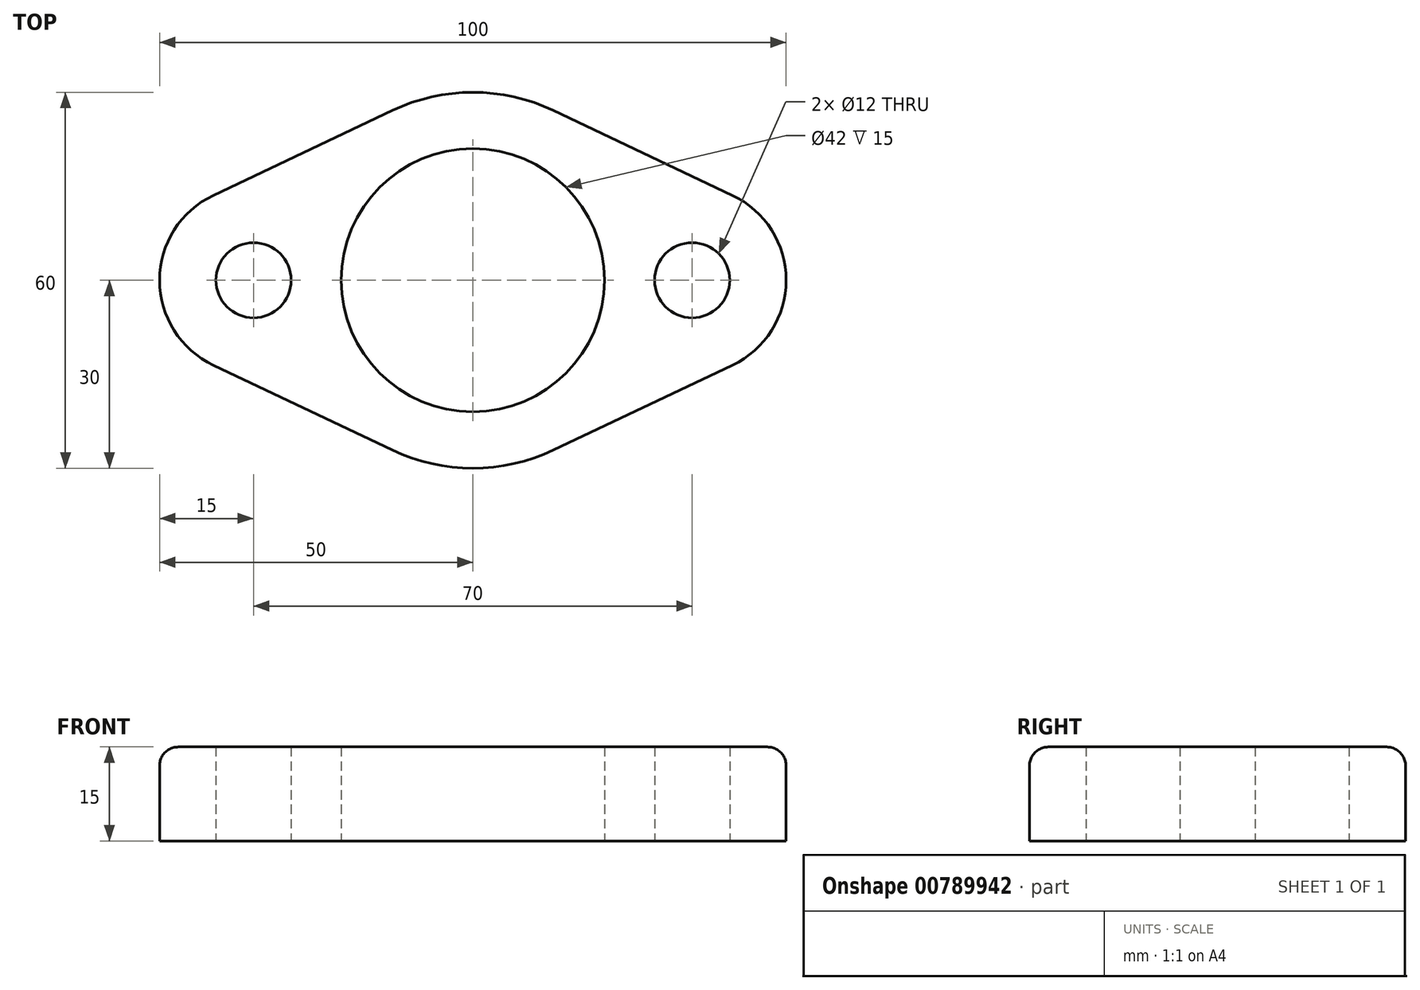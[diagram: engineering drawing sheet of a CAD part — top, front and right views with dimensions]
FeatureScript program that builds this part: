
annotation { "Feature Type Name" : "Feature", "Feature Type Description" : "" }
export const myFeature = defineFeature(function(context is Context, id is Id, definition is map)
    precondition{}
    {
        {
            var Q0;
            Q0=qCreatedBy(makeId("Top.planeOp"),FACE);
            var sketch = newSketch(context, id + "F0", { "sketchPlane" : qUnion([Q0])});
            skCircle(sketch, "E0", {"center": v(0, 0) * mm, "radius": 21 * mm});
            skArc(sketch, "E1", {"start": v(41.43, -13.55) * mm, "mid": v(50, 0) * mm, "end": v(41.43, 13.55) * mm});
            skCircle(sketch, "E2", {"center": v(35, 0) * mm, "radius": 6 * mm});
            skArc(sketch, "E3.MirrorC", {"start": v(-41.43, -13.55) * mm, "mid": v(-50, 0) * mm, "end": v(-41.43, 13.55) * mm});
            skCircle(sketch, "E4.MirrorC", {"center": v(-35, 0) * mm, "radius": 6 * mm});
            skLineSegment(sketch, "E5", {"start": v(-44.94, 11.89) * mm, "end": v(-12.86, 27.1) * mm});
            skLineSegment(sketch, "E6.MirrorCS", {"start": v(-44.94, -11.89) * mm, "end": v(-12.86, -27.1) * mm});
            skLineSegment(sketch, "E7.MirrorCS", {"start": v(44.94, 11.89) * mm, "end": v(12.86, 27.1) * mm});
            skLineSegment(sketch, "E8.MirrorCS", {"start": v(44.94, -11.89) * mm, "end": v(12.86, -27.1) * mm});
            skArc(sketch, "E9.trimOffspring", {"start": v(-12.86, -27.1) * mm, "mid": v(0, -30) * mm, "end": v(12.86, -27.1) * mm});
            skArc(sketch, "E10.trimOffspring", {"start": v(12.86, 27.1) * mm, "mid": v(0, 30) * mm, "end": v(-12.86, 27.1) * mm});
            skSolve(sketch);
        }
        {
            var Q0;
            Q0=makeQuery(id+"F0.imprint","IMPRINT",FACE,{"disambiguationData":[TD([[makeQuery(id+"F0.imprint","IMPRINT",EDGE,{"derivedFrom":sQuery(id+"F0.wireOp",EDGE,"E0")}),-1.0]])]});
            extrude(context, id + "F1", {"entities" : qUnion([Q0]), "depth" : 15 * mm, "offsetDistance" : 25 * mm});
        }
        {
            var Q0;
            Q0=makeQuery(id+"F1.opExtrude","CAP_EDGE",EDGE,{"disambiguationData":[OSD([sQuery(id+"F0.wireOp",EDGE,"E6.MirrorCS")])],"isStart":false});
            var Q1;
            Q1=makeQuery(id+"F1.opExtrude","CAP_EDGE",EDGE,{"disambiguationData":[OSD([sQuery(id+"F0.wireOp",EDGE,"E3.MirrorC")])],"isStart":false});
            var Q2;
            Q2=makeQuery(id+"F1.opExtrude","CAP_EDGE",EDGE,{"disambiguationData":[OSD([sQuery(id+"F0.wireOp",EDGE,"E5")])],"isStart":false});
            var Q3;
            Q3=makeQuery(id+"F1.opExtrude","CAP_EDGE",EDGE,{"disambiguationData":[OSD([sQuery(id+"F0.wireOp",EDGE,"E10.trimOffspring")])],"isStart":false});
            var Q4;
            Q4=makeQuery(id+"F1.opExtrude","CAP_EDGE",EDGE,{"disambiguationData":[OSD([sQuery(id+"F0.wireOp",EDGE,"E7.MirrorCS")])],"isStart":false});
            var Q5;
            Q5=makeQuery(id+"F1.opExtrude","CAP_EDGE",EDGE,{"disambiguationData":[OSD([sQuery(id+"F0.wireOp",EDGE,"E1")])],"isStart":false});
            var Q6;
            Q6=makeQuery(id+"F1.opExtrude","CAP_EDGE",EDGE,{"disambiguationData":[OSD([sQuery(id+"F0.wireOp",EDGE,"E8.MirrorCS")])],"isStart":false});
            var Q7;
            Q7=makeQuery(id+"F1.opExtrude","CAP_EDGE",EDGE,{"disambiguationData":[OSD([sQuery(id+"F0.wireOp",EDGE,"E9.trimOffspring")])],"isStart":false});
            fillet(context, id + "F2", {"entities" : qUnion([Q0, Q1, Q2, Q3, Q4, Q5, Q6, Q7]), "radius" : 3 * mm, "tangentPropagation" : true, "allowEdgeOverflow" : false});
        }
    });
